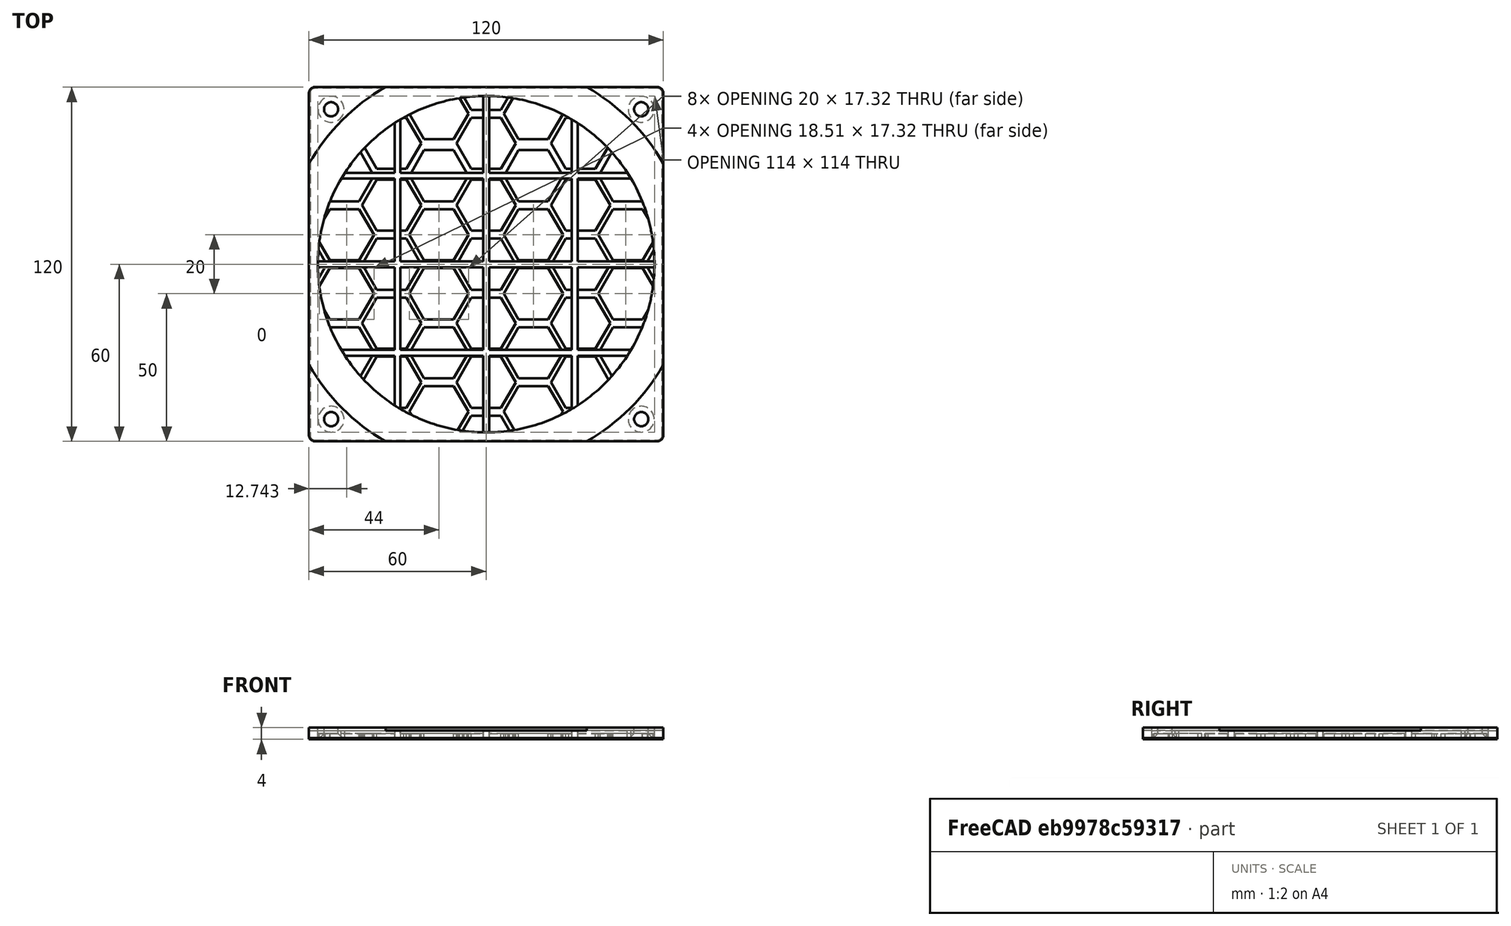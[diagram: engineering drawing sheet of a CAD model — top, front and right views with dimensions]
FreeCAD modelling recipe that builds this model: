
FCSTD DOCUMENT  (FreeCAD 0.18R14555 (Git shallow))
Label: 120mm-fan-guard
License: All rights reserved
LicenseURL: http://en.wikipedia.org/wiki/All_rights_reserved
objects: Part::Feature×21, Part::Box×7, Part::Cylinder×7, Part::MultiFuse×7, Part::Cut×4, Part::Chamfer×2, Part::MultiCommon×1, Part::Fillet×1
note: 50 computed .brp shape members not serialized (recipe doc carries the construction recipe); baked Part::Feature solids carry a one-line shape summary decoded from their .brp

FEATURE [Part::Box] Box  label="Cube"
  AttacherType = Attacher::AttachEngine3D
  Height = 4
  Length = 120
  Placement = pos=(-60,-60,0) rot=(0,0,1;0rad)
  Width = 120
FEATURE [Part::Cylinder] Cylinder
  Angle = 360
  AttacherType = Attacher::AttachEngine3D
  Height = 10
  Placement = pos=(0,0,2) rot=(0,0,1;0rad)
  Radius = 57
FEATURE [Part::Cut] Cut
  Base = -> Box
  Tool = -> Cylinder
FEATURE [Part::Box] Box001  label="Cube001"
  AttacherType = Attacher::AttachEngine3D
  Height = 3
  Length = 120
  Placement = pos=(-60,-1,0) rot=(0,0,1;0rad)
  Width = 2
FEATURE [Part::Box] Box002  label="Cube002"
  AttacherType = Attacher::AttachEngine3D
  Height = 3
  Length = 120
  Placement = pos=(-60,29,0) rot=(0,0,1;0rad)
  Width = 2
FEATURE [Part::Box] Box003  label="Cube003"
  AttacherType = Attacher::AttachEngine3D
  Height = 3
  Length = 120
  Placement = pos=(-60,-31,0) rot=(0,0,1;0rad)
  Width = 2
FEATURE [Part::Feature] Pad001  label="hex"
  shape: bbox 20 x 17.32 x 10 mm, 8 faces (baked)
FEATURE [Part::Feature] Pad002  label="hex001"
  Placement = pos=(32,0,0) rot=(0,0,1;0rad)
  shape: bbox 20 x 17.32 x 10 mm, 8 faces (baked)
FEATURE [Part::Feature] Pad003  label="hex002"
  Placement = pos=(16,10,0) rot=(0,0,1;0rad)
  shape: bbox 20 x 17.32 x 10 mm, 8 faces (baked)
FEATURE [Part::Feature] Pad004  label="hex003"
  Placement = pos=(-32,0,0) rot=(0,0,1;0rad)
  shape: bbox 20 x 17.32 x 10 mm, 8 faces (baked)
FEATURE [Part::Feature] Pad005  label="hex004"
  Placement = pos=(64,0,0) rot=(0,0,1;0rad)
  shape: bbox 20 x 17.32 x 10 mm, 8 faces (baked)
FEATURE [Part::Feature] Pad006  label="hex005"
  Placement = pos=(48,10,0) rot=(0,0,1;0rad)
  shape: bbox 20 x 17.32 x 10 mm, 8 faces (baked)
FEATURE [Part::Feature] Pad007  label="hex006"
  Placement = pos=(-16,10,0) rot=(0,0,1;0rad)
  shape: bbox 20 x 17.32 x 10 mm, 8 faces (baked)
FEATURE [Part::Feature] Pad008  label="hex007"
  Placement = pos=(-48,10,0) rot=(0,0,1;0rad)
  shape: bbox 20 x 17.32 x 10 mm, 8 faces (baked)
FEATURE [Part::Feature] Pad009  label="hex008"
  Placement = pos=(-64,0,0) rot=(0,0,1;0rad)
  shape: bbox 20 x 17.32 x 10 mm, 8 faces (baked)
FEATURE [Part::MultiFuse] Fusion001
  Shapes = -> [Pad009,Pad004,Pad001,Pad002,Pad005]
FEATURE [Part::MultiFuse] Fusion002
  Shapes = -> [Pad008,Pad007,Pad003,Pad006]
FEATURE [Part::Feature] Fusion002001  label="Fusion003"
  Placement = pos=(0,-20,0) rot=(0,0,1;0rad)
  shape: bbox 116 x 17.32 x 10 mm, 32 faces, 4 solids (baked)
FEATURE [Part::Feature] Fusion001001  label="Fusion004"
  Placement = pos=(0,-20,0) rot=(0,0,1;0rad)
  shape: bbox 148 x 17.32 x 10 mm, 40 faces, 5 solids (baked)
FEATURE [Part::Feature] Fusion002002  label="Fusion005"
  Placement = pos=(0,-40,0) rot=(0,0,1;0rad)
  shape: bbox 116 x 17.32 x 10 mm, 32 faces, 4 solids (baked)
FEATURE [Part::Feature] Fusion002003  label="Fusion006"
  Placement = pos=(0,-40,0) rot=(0,0,1;0rad)
  shape: bbox 148 x 17.32 x 10 mm, 40 faces, 5 solids (baked)
FEATURE [Part::Feature] Fusion002004  label="Fusion007"
  Placement = pos=(0,-60,0) rot=(0,0,1;0rad)
  shape: bbox 116 x 17.32 x 10 mm, 32 faces, 4 solids (baked)
FEATURE [Part::Feature] Fusion002005  label="Fusion008"
  Placement = pos=(0,-60,0) rot=(0,0,1;0rad)
  shape: bbox 148 x 17.32 x 10 mm, 40 faces, 5 solids (baked)
FEATURE [Part::Feature] Fusion002006  label="Fusion009"
  Placement = pos=(0,20,0) rot=(0,0,1;0rad)
  shape: bbox 116 x 17.32 x 10 mm, 32 faces, 4 solids (baked)
FEATURE [Part::Feature] Fusion001002  label="Fusion010"
  Placement = pos=(0,20,0) rot=(0,0,1;0rad)
  shape: bbox 148 x 17.32 x 10 mm, 40 faces, 5 solids (baked)
FEATURE [Part::Feature] Fusion002007  label="Fusion011"
  Placement = pos=(0,41,0) rot=(0,0,1;0rad)
  shape: bbox 148 x 17.32 x 10 mm, 40 faces, 5 solids (baked)
FEATURE [Part::Feature] Fusion002008  label="Fusion012"
  Placement = pos=(0,41,0) rot=(0,0,1;0rad)
  shape: bbox 116 x 17.32 x 10 mm, 32 faces, 4 solids (baked)
FEATURE [Part::Feature] Fusion002009  label="Fusion013"
  Placement = pos=(0,61,0) rot=(0,0,1;0rad)
  shape: bbox 148 x 17.32 x 10 mm, 40 faces, 5 solids (baked)
FEATURE [Part::MultiFuse] Fusion002010
  Shapes = -> [Fusion002009,Fusion002001,Fusion002,Fusion002007,Fusion001001,Fusion002003,Fusion001,Fusion002004,Fusion002002,Fusion002008,Fusion002005,Fusion001002,Fusion002006]
FEATURE [Part::Cylinder] Cylinder001
  Angle = 360
  AttacherType = Attacher::AttachEngine3D
  Height = 10
  Radius = 57
FEATURE [Part::MultiCommon] Common
  Shapes = -> [Fusion002010,Cylinder001]
FEATURE [Part::MultiFuse] Fusion
  Shapes = -> [Box001,Box002,Box003]
FEATURE [Part::Cut] Cut001
  Base = -> Cut
  Tool = -> Common
FEATURE [Part::MultiFuse] Fusion002011
  Shapes = -> [Cut001,Fusion]
FEATURE [Part::Cylinder] Cylinder002
  Angle = 360
  AttacherType = Attacher::AttachEngine3D
  Height = 10
  Placement = pos=(-52.5,52.5,0) rot=(0,0,1;0rad)
  Radius = 2.4
FEATURE [Part::Cylinder] Cylinder003
  Angle = 360
  AttacherType = Attacher::AttachEngine3D
  Height = 10
  Placement = pos=(52.5,52.5,0) rot=(0,0,1;0rad)
  Radius = 2.4
FEATURE [Part::Cylinder] Cylinder004
  Angle = 360
  AttacherType = Attacher::AttachEngine3D
  Height = 10
  Placement = pos=(-52.5,-52.5,0) rot=(0,0,1;0rad)
  Radius = 2.4
FEATURE [Part::Cylinder] Cylinder005
  Angle = 360
  AttacherType = Attacher::AttachEngine3D
  Height = 10
  Placement = pos=(52.5,-52.5,0) rot=(0,0,1;0rad)
  Radius = 2.4
FEATURE [Part::Box] Box004  label="Cube004"
  AttacherType = Attacher::AttachEngine3D
  Height = 3
  Length = 2
  Placement = pos=(-1,-60,0) rot=(0,0,1;0rad)
  Width = 120
FEATURE [Part::Box] Box005  label="Cube005"
  AttacherType = Attacher::AttachEngine3D
  Height = 3
  Length = 2
  Placement = pos=(-31,-60,0) rot=(0,0,1;0rad)
  Width = 120
FEATURE [Part::Box] Box006  label="Cube006"
  AttacherType = Attacher::AttachEngine3D
  Height = 3
  Length = 2
  Placement = pos=(29,-60,0) rot=(0,0,1;0rad)
  Width = 120
FEATURE [Part::MultiFuse] Fusion002013
  Shapes = -> [Fusion002011,Box004,Box005,Box006]
FEATURE [Part::MultiFuse] Fusion002014
  Shapes = -> [Cylinder002,Cylinder003,Cylinder005,Cylinder004]
FEATURE [Part::Cut] Cut002
  Base = -> Fusion002013
  Tool = -> Fusion002014
FEATURE [Part::Chamfer] Chamfer
  Base = -> Cut002
  Edges = 4 edges r=2: [Edge86,Edge99,Edge363,Edge534]
FEATURE [Part::Fillet] Fillet
  Base = -> Chamfer
  Edges = 4 edges r=2: [Edge16,Edge29,Edge42,Edge131]
FEATURE [Part::Feature] Fillet001
  shape: bbox 120 x 120 x 4 mm, 310 faces (baked)
FEATURE [Part::Chamfer] Chamfer001
  Base = -> Fillet001
  Edges = 8 edges r=0.4: [Edge6,Edge61,Edge64,Edge67,Edge82,Edge83,Edge84,Edge85]
FEATURE [Part::Cylinder] Cylinder006
  Angle = 360
  AttacherType = Attacher::AttachEngine3D
  Height = 10
  Placement = pos=(0,0,3) rot=(0,0,1;0rad)
  Radius = 69
FEATURE [Part::Cut] Cut003
  Base = -> Chamfer001
  Tool = -> Cylinder006
